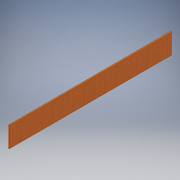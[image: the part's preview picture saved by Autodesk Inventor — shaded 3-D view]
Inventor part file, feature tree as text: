
AUTODESK INVENTOR PART (.ipt)
format: ipt  version: 2016 (Build 200138000, 138)  size: 107,520 bytes
history: native  units: in
note: dims shown in document units (in); Inventor stores cm internally (conversion verified against a paired STEP export)
features: extrude x1, fillet x1, sketch x1
ambient origin geometry x8: Origin, YZ Plane, XZ Plane, XY Plane, X Axis, Y Axis, Z Axis, Center Point
bodies: Solid1 (feature_tree)
feature tree (3):
  extrude  "Extrusion1"  Depth=6.5in
  fillet  "Fillet1"  Radius=0.4375in
  sketch  "Sketch1"  dims[d0=51.5in d1=6.5in d2=0.4375in d3=0.0in d4=0.125in]
